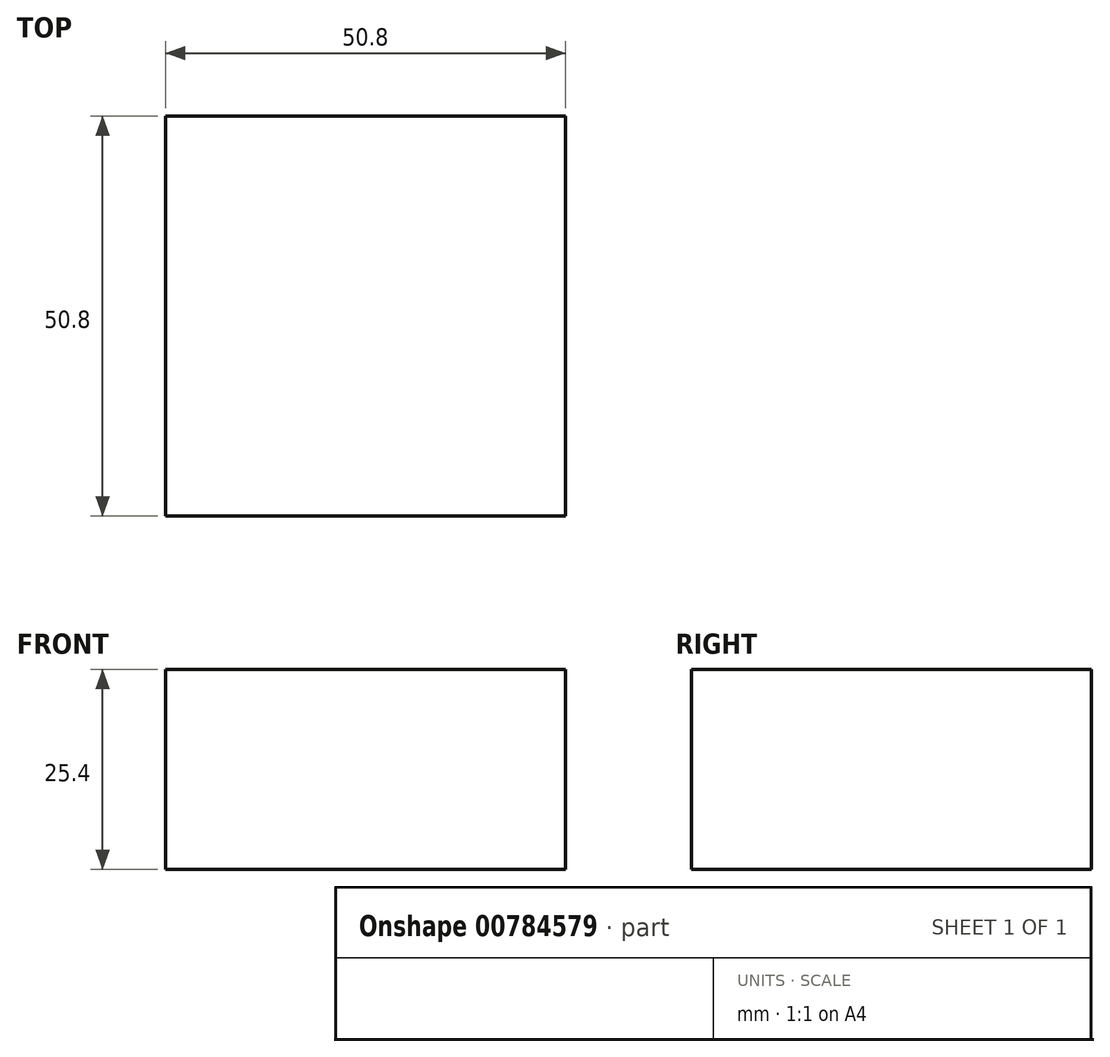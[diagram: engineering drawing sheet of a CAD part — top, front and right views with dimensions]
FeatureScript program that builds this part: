
annotation { "Feature Type Name" : "Feature", "Feature Type Description" : "" }
export const myFeature = defineFeature(function(context is Context, id is Id, definition is map)
    precondition{}
    {
        {
            var Q0;
            Q0=qCreatedBy(makeId("Top.planeOp"),FACE);
            var sketch = newSketch(context, id + "F0", { "sketchPlane" : qUnion([Q0])});
            skLineSegment(sketch, "E0.bottom", {"start": v(-36.57, -26.83) * mm, "end": v(14.23, -26.83) * mm});
            skLineSegment(sketch, "E0.top", {"start": v(-36.57, 23.97) * mm, "end": v(14.23, 23.97) * mm});
            skLineSegment(sketch, "E0.left", {"start": v(-36.57, -26.83) * mm, "end": v(-36.57, 23.97) * mm});
            skLineSegment(sketch, "E0.right", {"start": v(14.23, -26.83) * mm, "end": v(14.23, 23.97) * mm});
            skSolve(sketch);
        }
        {
            var Q0;
            Q0 = qSketchRegion(id + "F0", true);
            extrude(context, id + "F1", {"entities" : qUnion([Q0]), "depth" : 25.4 * mm, "offsetDistance" : 25.4 * mm});
        }
    });
